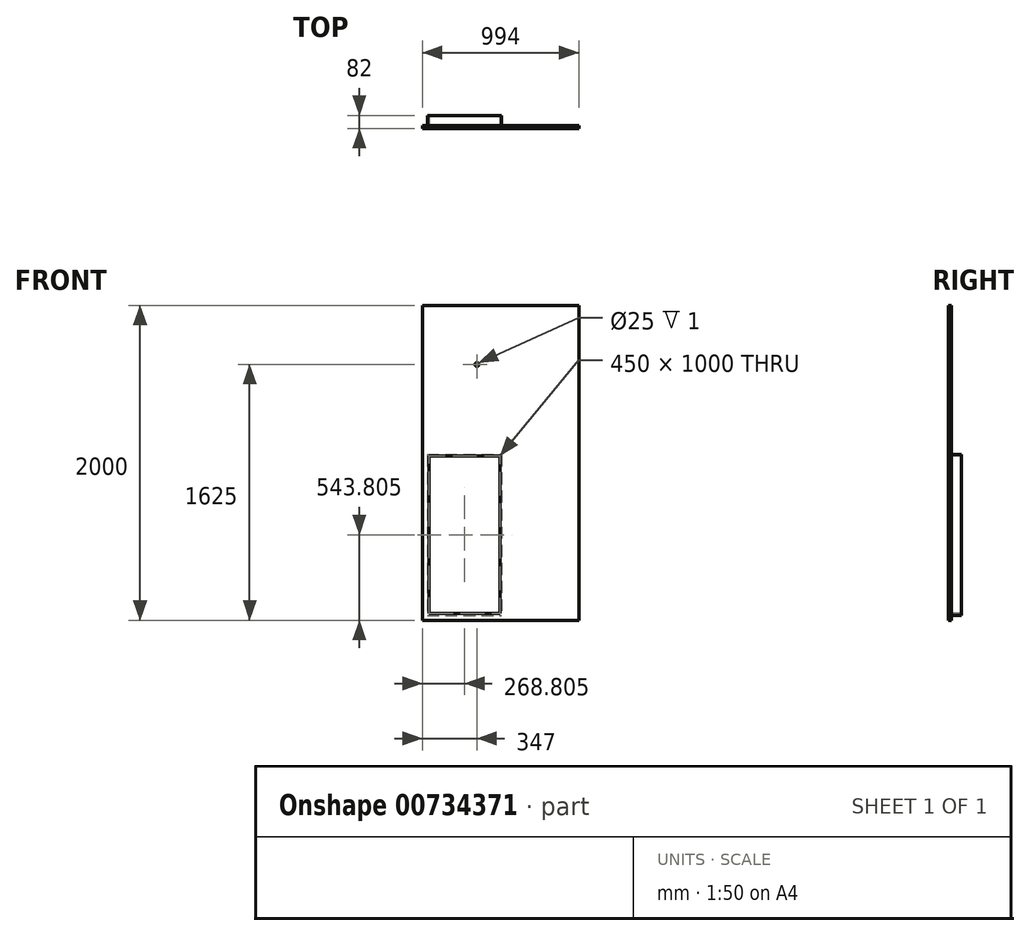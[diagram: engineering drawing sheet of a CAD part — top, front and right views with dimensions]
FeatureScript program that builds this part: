
annotation { "Feature Type Name" : "Feature", "Feature Type Description" : "" }
export const myFeature = defineFeature(function(context is Context, id is Id, definition is map)
    precondition{}
    {
        {
            var Q0;
            Q0=qCreatedBy(makeId("Front.planeOp"),FACE);
            var sketch = newSketch(context, id + "F0", { "sketchPlane" : qUnion([Q0])});
            skLineSegment(sketch, "E0.bottom", {"start": v(-497, -1000) * mm, "end": v(497, -1000) * mm});
            skLineSegment(sketch, "E0.top", {"start": v(-497, 1000) * mm, "end": v(497, 1000) * mm});
            skLineSegment(sketch, "E0.left", {"start": v(-497, -1000) * mm, "end": v(-497, 1000) * mm});
            skLineSegment(sketch, "E0.right", {"start": v(497, -1000) * mm, "end": v(497, 1000) * mm});
            skPoint(sketch, "E0.middle", {"position": v(0, 0) * mm});
            skSolve(sketch);
        }
        {
            var Q0;
            Q0=qSketchRegion(id+"F0",true);
            extrude(context, id + "F1", {"entities" : qUnion([Q0]), "oppositeDirection" : true, "depth" : 18 * mm, "offsetDistance" : 25 * mm});
        }
        {
            var Q0;
            Q0=makeQuery(id+"F1.opExtrude","CAP_FACE",FACE,{"disambiguationData":[OSD([sQuery(id+"F0.wireOp",EDGE,"E0.bottom"),sQuery(id+"F0.wireOp",EDGE,"E0.top"),sQuery(id+"F0.wireOp",EDGE,"E0.left"),sQuery(id+"F0.wireOp",EDGE,"E0.right")])],"isStart":true});
            var sketch = newSketch(context, id + "F2", { "sketchPlane" : qUnion([Q0])});
            skLineSegment(sketch, "E1", {"start": v(497, 625) * mm, "end": v(297, 625) * mm, "construction": true});
            skLineSegment(sketch, "E2", {"start": v(297, 625) * mm, "end": v(197, 625) * mm, "construction": true});
            skLineSegment(sketch, "E3", {"start": v(197, 625) * mm, "end": v(-497, 625) * mm, "construction": true});
            skCircle(sketch, "E4", {"center": v(-150, 625) * mm, "radius": 12.5 * mm});
            skSolve(sketch);
        }
        {
            var Q0;
            Q0 = qSketchRegion(id + "F2", true);
            extrude(context, id + "F3", {"entities" : qUnion([Q0]), "operationType" : NewBodyOperationType.REMOVE, "oppositeDirection" : true, "depth" : 1 * mm, "offsetDistance" : 25 * mm});
        }
        {
            var Q0;
            Q0=makeQuery(id+"F1.opExtrude","CAP_FACE",FACE,{"disambiguationData":[OSD([sQuery(id+"F0.wireOp",EDGE,"E0.bottom"),sQuery(id+"F0.wireOp",EDGE,"E0.top"),sQuery(id+"F0.wireOp",EDGE,"E0.left"),sQuery(id+"F0.wireOp",EDGE,"E0.right")])],"isStart":true});
            var sketch = newSketch(context, id + "F4", { "sketchPlane" : qUnion([Q0])});
            skLineSegment(sketch, "E5.bottom", {"start": v(-453.2, -956.2) * mm, "end": v(-3.2, -956.2) * mm});
            skLineSegment(sketch, "E5.top", {"start": v(-453.2, 43.8) * mm, "end": v(-3.2, 43.8) * mm});
            skLineSegment(sketch, "E5.left", {"start": v(-453.2, -956.2) * mm, "end": v(-453.2, 43.8) * mm});
            skLineSegment(sketch, "E5.right", {"start": v(-3.2, -956.2) * mm, "end": v(-3.2, 43.8) * mm});
            skLineSegment(sketch, "E6", {"start": v(297, -1000) * mm, "end": v(297, 1000) * mm, "construction": true});
            skLineSegment(sketch, "E7", {"start": v(197, 1000) * mm, "end": v(197, -1000) * mm, "construction": true});
            skLineSegment(sketch, "E8", {"start": v(-228.2, -956.2) * mm, "end": v(-228.2, -1000) * mm, "construction": true});
            skLineSegment(sketch, "E9", {"start": v(-453.2, -456.2) * mm, "end": v(-497, -456.2) * mm, "construction": true});
            skSolve(sketch);
        }
        {
            var Q0;
            Q0 = qSketchRegion(id + "F4", true);
            extrude(context, id + "F5", {"entities" : qUnion([Q0]), "operationType" : NewBodyOperationType.REMOVE, "oppositeDirection" : true, "depth" : 82 * mm, "offsetDistance" : 25 * mm});
        }
        {
            var Q0;
            Q0=makeQuery(id+"F1.opExtrude","CAP_FACE",FACE,{"disambiguationData":[OSD([sQuery(id+"F0.wireOp",EDGE,"E0.bottom"),sQuery(id+"F0.wireOp",EDGE,"E0.top"),sQuery(id+"F0.wireOp",EDGE,"E0.left"),sQuery(id+"F0.wireOp",EDGE,"E0.right")])],"isStart":true});
            var sketch = newSketch(context, id + "F6", { "sketchPlane" : qUnion([Q0])});
            skLineSegment(sketch, "E10.bottom", {"start": v(-465.32, 53.86) * mm, "end": v(5.74, 53.86) * mm});
            skLineSegment(sketch, "E10.top", {"start": v(-465.32, -969.06) * mm, "end": v(5.74, -969.06) * mm});
            skLineSegment(sketch, "E10.left", {"start": v(-465.32, 53.86) * mm, "end": v(-465.32, -969.06) * mm});
            skLineSegment(sketch, "E10.right", {"start": v(5.74, 53.86) * mm, "end": v(5.74, -969.06) * mm});
            skLineSegment(sketch, "E11.0", {"start": v(-453.2, -956.2) * mm, "end": v(-453.2, 43.8) * mm});
            skLineSegment(sketch, "E12.0", {"start": v(-453.2, -956.2) * mm, "end": v(-3.2, -956.2) * mm});
            skLineSegment(sketch, "E13.0", {"start": v(-3.2, -956.2) * mm, "end": v(-3.2, 43.8) * mm});
            skLineSegment(sketch, "E14.0", {"start": v(-453.2, 43.8) * mm, "end": v(-3.2, 43.8) * mm});
            skSolve(sketch);
        }
        {
            var Q0;
            Q0=makeQuery(id+"F6.imprint","IMPRINT",FACE,{"disambiguationData":[TD([[makeQuery(id+"F6.imprint","IMPRINT",EDGE,{"derivedFrom":sQuery(id+"F6.wireOp",EDGE,"E10.bottom")}),-1.0]])]});
            extrude(context, id + "F7", {"entities" : qUnion([Q0]), "operationType" : NewBodyOperationType.ADD, "oppositeDirection" : true, "depth" : 82 * mm, "offsetDistance" : 25 * mm});
        }
    });
